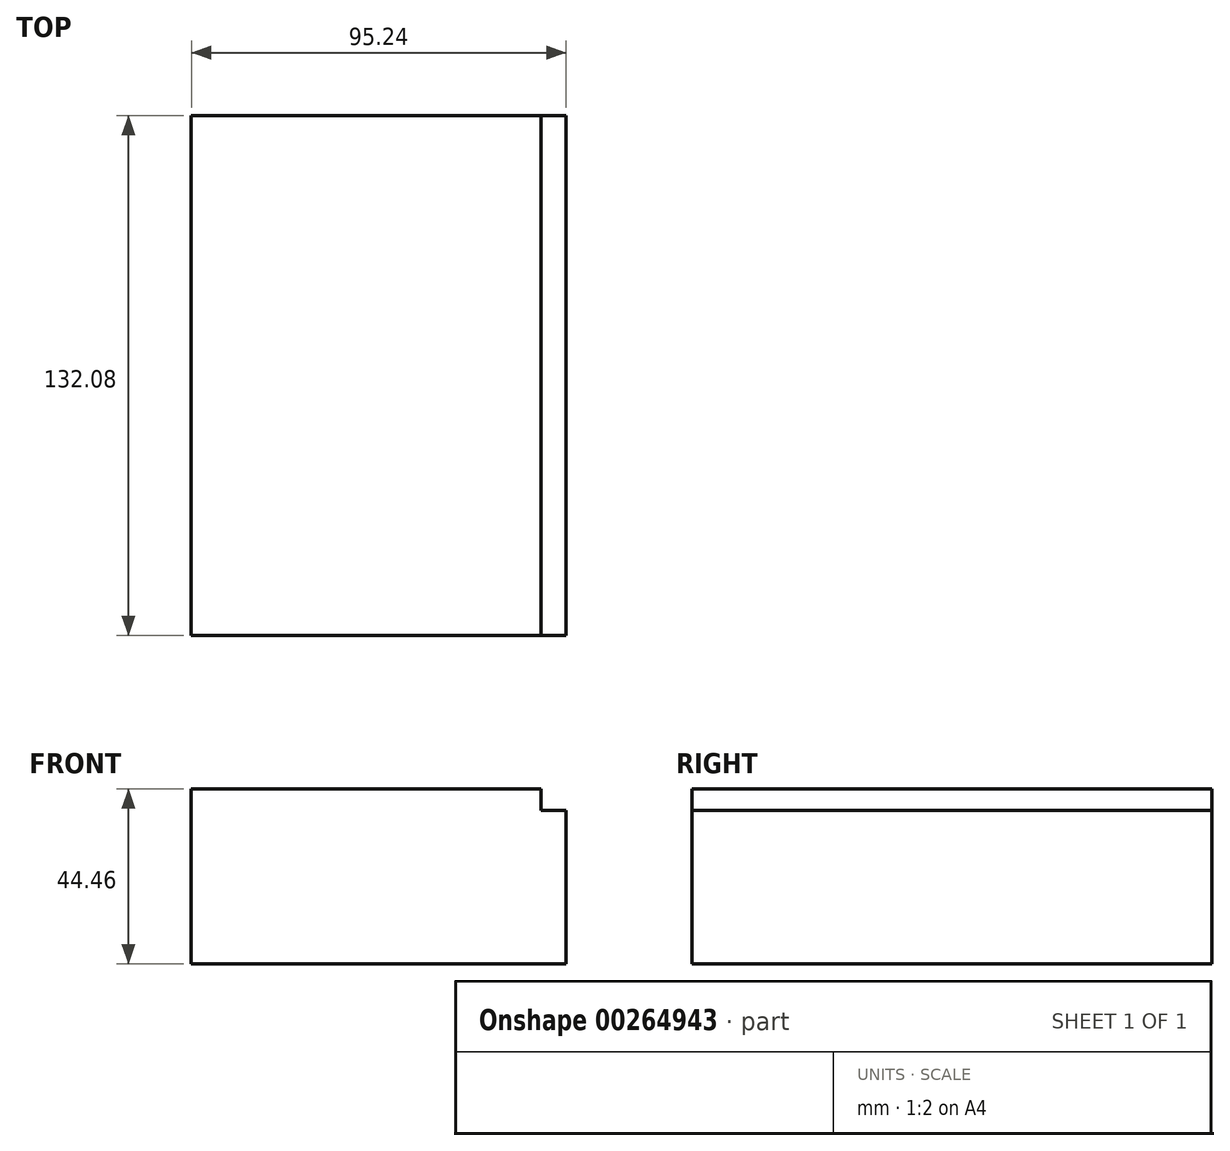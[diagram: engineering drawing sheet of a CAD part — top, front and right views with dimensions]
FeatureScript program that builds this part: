
annotation { "Feature Type Name" : "Feature", "Feature Type Description" : "" }
export const myFeature = defineFeature(function(context is Context, id is Id, definition is map)
    precondition{}
    {
        {
            var Q0;
            Q0=qCreatedBy(makeId("Front.planeOp"),FACE);
            var sketch = newSketch(context, id + "F0", { "sketchPlane" : qUnion([Q0])});
            skLineSegment(sketch, "E0.bottom", {"start": v(47.63, -22.22) * mm, "end": v(-47.62, -22.23) * mm});
            skLineSegment(sketch, "E0.top", {"start": v(47.62, 22.23) * mm, "end": v(-47.63, 22.22) * mm});
            skLineSegment(sketch, "E0.left", {"start": v(47.63, -22.22) * mm, "end": v(47.62, 22.23) * mm});
            skLineSegment(sketch, "E0.right", {"start": v(-47.62, -22.23) * mm, "end": v(-47.63, 22.22) * mm});
            skPoint(sketch, "E0.middle", {"position": v(0, 0) * mm});
            skLineSegment(sketch, "E1.bottom", {"start": v(61.34, 75.44) * mm, "end": v(93.09, 75.44) * mm});
            skLineSegment(sketch, "E1.top", {"start": v(61.34, 50.04) * mm, "end": v(93.09, 50.04) * mm});
            skLineSegment(sketch, "E1.left", {"start": v(61.34, 75.44) * mm, "end": v(61.34, 50.04) * mm});
            skLineSegment(sketch, "E1.right", {"start": v(93.09, 75.44) * mm, "end": v(93.09, 50.04) * mm});
            skPoint(sketch, "E1.middle", {"position": v(77.21, 62.74) * mm});
            skLineSegment(sketch, "E2", {"start": v(47.62, 22.23) * mm, "end": v(47.62, 40.22) * mm});
            skArc(sketch, "E3", {"start": v(57.52, 51.35) * mm, "mid": v(50.46, 47.67) * mm, "end": v(47.62, 40.22) * mm});
            skLineSegment(sketch, "E4", {"start": v(57.52, 51.35) * mm, "end": v(79.78, 51.35) * mm});
            skLineSegment(sketch, "E5.0", {"start": v(41.28, 16.82) * mm, "end": v(41.28, 40.22) * mm});
            skArc(sketch, "E5.1", {"start": v(57.19, 57.7) * mm, "mid": v(45.85, 52.04) * mm, "end": v(41.27, 40.22) * mm});
            skLineSegment(sketch, "E5.2", {"start": v(57.19, 57.7) * mm, "end": v(79.78, 57.7) * mm});
            skLineSegment(sketch, "E6", {"start": v(79.78, 51.35) * mm, "end": v(79.78, 57.7) * mm});
            skLineSegment(sketch, "E7", {"start": v(41.28, 16.82) * mm, "end": v(47.62, 16.82) * mm});
            skFitSpline(sketch, "E8", {"points": [v(-47.63, 22.22) * mm, v(57.19, 57.7) * mm], "startDerivative": vector(44.94, 95.5) * mm, "endDerivative": vector(124.81, -10.39) * mm});
            skSolve(sketch);
        }
        {
            var Q0;
            {var subQ6=sQuery(id+"F0.wireOp",EDGE,"E0.bottom");Q0=makeQuery(id+"F0.imprint","IMPRINT",FACE,{"disambiguationData":[TD([[makeQuery(id+"F0.imprint","IMPRINT",EDGE,{"derivedFrom":subQ6}),-1.0]])]});}
            extrude(context, id + "F1", {"entities" : qUnion([Q0]), "endBound" : BoundingType.SYMMETRIC, "depth" : 106.68 * mm});
        }
        {
            var Q0;
            Q0=makeQuery(id+"F1.opExtrude","CAP_FACE",FACE,{"disambiguationData":[OSD([sQuery(id+"F0.wireOp",EDGE,"E0.bottom"),sQuery(id+"F0.wireOp",EDGE,"E0.top"),sQuery(id+"F0.wireOp",EDGE,"E0.left"),sQuery(id+"F0.wireOp",EDGE,"E0.right"),sQuery(id+"F0.wireOp",EDGE,"E5.0"),sQuery(id+"F0.wireOp",EDGE,"E7")])],"isStart":false});
            extrude(context, id + "F2", {"entities" : qUnion([Q0]), "operationType" : NewBodyOperationType.ADD, "depth" : 25.4 * mm});
        }
        {
            var Q0;
            {var subQ0=sQuery(id+"F0.wireOp",EDGE,"E0.top");Q0=makeQuery(id+"F2.boolean.opBoolean","MERGE",FACE,{"derivedFrom":[makeQuery(id+"F1.opExtrude","SWEPT_FACE",FACE,{"disambiguationData":[OSD([subQ0])]}),makeQuery(id+"F2.opExtrude","SWEPT_FACE",FACE,{"disambiguationData":[OSD([subQ0])]})]});}
            extrude(context, id + "F3", {"entities" : qUnion([Q0]), "operationType" : NewBodyOperationType.ADD, "oppositeDirection" : true, "depth" : 3.05 * mm});
        }
    });
